# Revit family: 3-654-xxx OPUS pendant
name_source: partatom
category: Lighting Fixtures
revit_build: Autodesk Revit 2018 (Build: 20170223_1515(x64)
units: mm (PartAtom-declared; Revit-internal decimal feet)

## family parameters
Always vertical = Yes
Cut with Voids When Loaded = No
Host = Ceiling
Light Source = Yes
OmniClass Number = 23.80.70.11
OmniClass Title = Luminaries for Internal Lighting
Part Type = Normal
Room Calculation Point = No
Round Connector Dimension = Use Diameter
Shared = No

## types (16) — shared parameters
Color Filter = 16777215
Dimming Lamp Color Temperature Shift = <None>
Input Voltage = 120 V or 277 V 50/60 Hz
Lamp = LED Array
Manufacturer = Oxygen Lighting
Model = 3-654-xxx / 37-654-xxx - OPUS pendant
Other 1 = Braided Cord
References = Ref. 3=120 V / Ref. 37= 277 V
Supplied with = Supplied with 8 ft of braided cord
Tilt Angle = 90.00°
URL = www.oxygenlighting.com

## per-type parameters (varying)
| type | Main Diffuser | Metal Finish | Photometric Web File | Voltage | Wattage Comments |
| 3-654-114 / Polished Chrome - Matte Opal Glass | White Opal Glass | 14 - Polished Chrome | 3-654-114 Opus Pendant.ies | 120 V | 6.72 W at 120 V |
| 37-654-114 / Polished Chrome - Matte Opal Glass | White Opal Glass | 14 - Polished Chrome | 3-654-114 Opus Pendant.ies | 277 V | 6.72 W at 120 V |
| 3-654-124 / Satin Nickel - Matte Opal Glass | White Opal Glass | 24 - Satin Nickel | 3-654-114 Opus Pendant.ies | 120 V | 6.72 W at 120 V |
| 37-654-124 / Satin Nickel - Matte Opal Glass | White Opal Glass | 24 - Satin Nickel | 3-654-114 Opus Pendant.ies | 277 V | 6.72 W at 120 V |
| 3-654-125 / Satin Cooper - Matte Opal Glass | White Opal Glass | 25 - Satin Copper | 3-654-114 Opus Pendant.ies | 120 V | 6.72 W at 120 V |
| 37-654-125 / Satin Cooper - Matte Opal Glass | White Opal Glass | 25 - Satin Copper | 3-654-114 Opus Pendant.ies | 277 V | 6.72 W at 120 V |
| 3-654-140 / Aged Brass - Matte Opal Glass | White Opal Glass | 40 - Aged Brass | 3-654-114 Opus Pendant.ies | 120 V | 6.72 W at 120 V |
| 37-654-140 / Aged Brass - Matte Opal Glass | White Opal Glass | 40 - Aged Brass | 3-654-114 Opus Pendant.ies | 277 V | 6.72 W at 120 V |
| 3-654-14 / Polished Chrome - Matte White Acrylic | Matte White Acrylic | 14 - Polished Chrome | 3-654-14 Opus Pendant.ies | 120 V | 6.69 W at 120 V |
| 37-654-14 / Polished Chrome - Matte White Acrylic | Matte White Acrylic | 14 - Polished Chrome | 3-654-14 Opus Pendant.ies | 277 V | 6.69 W at 120 V |
| 3-654-24 / Satin Nickel - Matte White Acrylic | Matte White Acrylic | 24 - Satin Nickel | 3-654-14 Opus Pendant.ies | 120 V | 6.69 W at 120 V |
| 37-654-24 / Satin Nickel - Matte White Acrylic | Matte White Acrylic | 24 - Satin Nickel | 3-654-14 Opus Pendant.ies | 277 V | 6.69 W at 120 V |
| 3-654-25 / Satin Cooper - Matte White Acrylic | Matte White Acrylic | 25 - Satin Copper | 3-654-14 Opus Pendant.ies | 120 V | 6.69 W at 120 V |
| 37-654-25 / Satin Cooper - Matte White Acrylic | Matte White Acrylic | 25 - Satin Copper | 3-654-14 Opus Pendant.ies | 277 V | 6.69 W at 120 V |
| 3-654-40 / Aged Brass - Matte White Acrylic | Matte White Acrylic | 40 - Aged Brass | 3-654-14 Opus Pendant.ies | 120 V | 6.69 W at 120 V |
| 37-654-40 / Aged Brass - Matte White Acrylic | Matte White Acrylic | 40 - Aged Brass | 3-654-14 Opus Pendant.ies | 277 V | 6.69 W at 120 V |

## geometry (parser evidence)
native form markers: Sweep x1
no freeform markers — native parametric forms only
